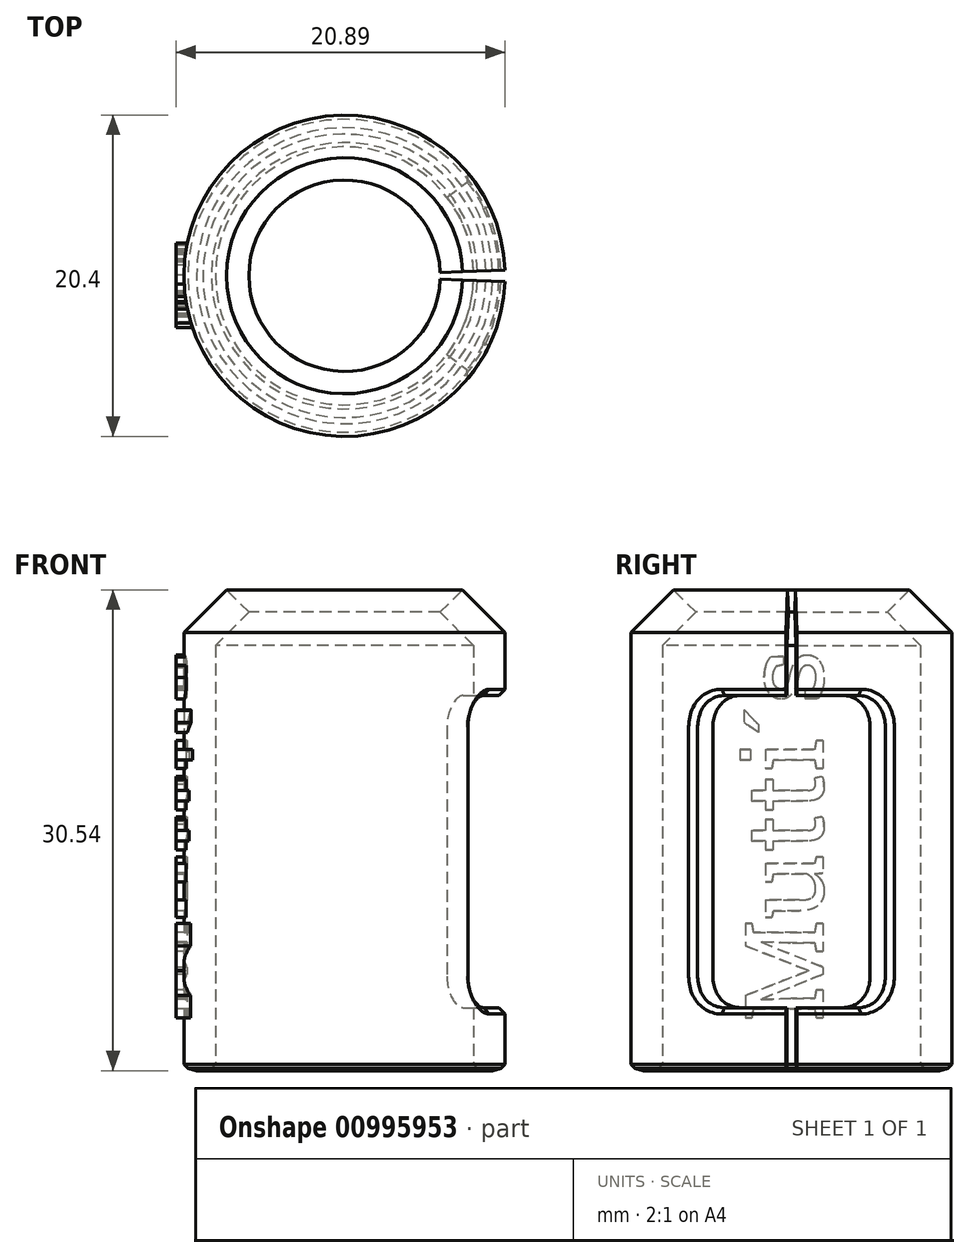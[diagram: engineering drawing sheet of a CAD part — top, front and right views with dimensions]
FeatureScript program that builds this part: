
annotation { "Feature Type Name" : "Feature", "Feature Type Description" : "" }
export const myFeature = defineFeature(function(context is Context, id is Id, definition is map)
    precondition{}
    {
        {
            var Q0;
            Q0=qCreatedBy(makeId("Front.planeOp"),FACE);
            var sketch = newSketch(context, id + "F0", { "sketchPlane" : qUnion([Q0])});
            skLineSegment(sketch, "E0", {"start": v(0, 0) * mm, "end": v(25.05, 0) * mm, "construction": true});
            skLineSegment(sketch, "E1", {"start": v(8.2, 0) * mm, "end": v(10.2, 0) * mm});
            skLineSegment(sketch, "E2", {"start": v(10.2, 0) * mm, "end": v(10.2, 27.83) * mm});
            skLineSegment(sketch, "E3", {"start": v(10.2, 27.83) * mm, "end": v(7.5, 30.54) * mm});
            skLineSegment(sketch, "E4", {"start": v(7.5, 30.54) * mm, "end": v(6.08, 29.12) * mm});
            skLineSegment(sketch, "E5", {"start": v(6.08, 29.12) * mm, "end": v(8.2, 27) * mm});
            skLineSegment(sketch, "E6", {"start": v(8.2, 27) * mm, "end": v(8.2, 0) * mm});
            skLineSegment(sketch, "E7", {"start": v(0, 0) * mm, "end": v(0, 50.76) * mm, "construction": true});
            skLineSegment(sketch, "E8", {"start": v(0, 11.1) * mm, "end": v(10.2, 11.1) * mm, "construction": true});
            skLineSegment(sketch, "E9", {"start": v(0, 11.1) * mm, "end": v(-10.2, 11.1) * mm, "construction": true});
            skLineSegment(sketch, "E10", {"start": v(-10.2, 11.1) * mm, "end": v(-20.4, 11.1) * mm, "construction": true});
            skSolve(sketch);
        }
        {
            var Q0;
            Q0 = qSketchRegion(id + "F0", true);
            var Q1;
            Q1=sQuery(id+"F0.wireOp",EDGE,"E7");
            revolve(context, id + "F1", {"surfaceOperationType" : NewSurfaceOperationType.NEW, "entities" : qUnion([Q0]), "axis" : qUnion([Q1]), "revolveType" : RevolveType.FULL});
        }
        {
            var Q0;
            Q0=qCreatedBy(makeId("Front.planeOp"),FACE);
            var sketch = newSketch(context, id + "F2", { "sketchPlane" : qUnion([Q0])});
            skLineSegment(sketch, "E11.top", {"start": v(0, 23.83) * mm, "end": v(20, 23.83) * mm});
            skLineSegment(sketch, "E11.left", {"start": v(0, 4) * mm, "end": v(0, 23.83) * mm});
            skLineSegment(sketch, "E11.right", {"start": v(20, 4) * mm, "end": v(20, 23.83) * mm});
            skLineSegment(sketch, "E12", {"start": v(0, 4) * mm, "end": v(20, 4) * mm});
            skSolve(sketch);
        }
        {
            var Q0;
            Q0 = qSketchRegion(id + "F2", true);
            var Q1;
            Q1=sQuery(id+"F2.wireOp",EDGE,"E11.left");
            revolve(context, id + "F3", {"operationType" : NewBodyOperationType.REMOVE, "surfaceOperationType" : NewSurfaceOperationType.NEW, "entities" : qUnion([Q0]), "axis" : qUnion([Q1]), "revolveType" : RevolveType.SYMMETRIC, "oppositeDirection" : true, "angle" : 75 * degree});
        }
        {
            var Q0;
            Q0=makeQuery(id+"F3.boolean.opBoolean","COPY",EDGE,{"derivedFrom":makeQuery(id+"F3.opRevolve","CAP_EDGE",EDGE,{"disambiguationData":[OSD([sQuery(id+"F2.wireOp",EDGE,"E12")])],"isStart":true})});
            var Q1;
            Q1=makeQuery(id+"F3.boolean.opBoolean","COPY",EDGE,{"derivedFrom":makeQuery(id+"F3.opRevolve","CAP_EDGE",EDGE,{"disambiguationData":[OSD([sQuery(id+"F2.wireOp",EDGE,"E12")])],"isStart":false})});
            var Q2;
            Q2=makeQuery(id+"F3.boolean.opBoolean","COPY",EDGE,{"derivedFrom":makeQuery(id+"F3.opRevolve","CAP_EDGE",EDGE,{"disambiguationData":[OSD([sQuery(id+"F2.wireOp",EDGE,"E11.top")])],"isStart":true})});
            var Q3;
            Q3=makeQuery(id+"F3.boolean.opBoolean","COPY",EDGE,{"derivedFrom":makeQuery(id+"F3.opRevolve","CAP_EDGE",EDGE,{"disambiguationData":[OSD([sQuery(id+"F2.wireOp",EDGE,"E11.top")])],"isStart":false})});
            fillet(context, id + "F4", {"entities" : qUnion([Q0, Q1, Q2, Q3]), "radius" : 2 * mm, "tangentPropagation" : true, "allowEdgeOverflow" : false});
        }
        {
            var Q0;
            Q0=qCreatedBy(makeId("Front.planeOp"),FACE);
            var sketch = newSketch(context, id + "F5", { "sketchPlane" : qUnion([Q0])});
            skLineSegment(sketch, "E13.bottom", {"start": v(0, 36.41) * mm, "end": v(18, 36.41) * mm});
            skLineSegment(sketch, "E13.top", {"start": v(0, -8.25) * mm, "end": v(18, -8.25) * mm});
            skLineSegment(sketch, "E13.left", {"start": v(0, 36.41) * mm, "end": v(0, -8.25) * mm});
            skLineSegment(sketch, "E13.right", {"start": v(18, 36.41) * mm, "end": v(18, -8.25) * mm});
            skSolve(sketch);
        }
        {
            var Q0;
            Q0 = qSketchRegion(id + "F5", true);
            var Q1;
            Q1=sQuery(id+"F0.wireOp",EDGE,"E7");
            revolve(context, id + "F6", {"operationType" : NewBodyOperationType.REMOVE, "surfaceOperationType" : NewSurfaceOperationType.NEW, "entities" : qUnion([Q0]), "axis" : qUnion([Q1]), "revolveType" : RevolveType.SYMMETRIC, "angle" : 4 * degree});
        }
        {
            var Q0;
            Q0=sQuery(id+"F0.wireOp",VERTEX,"E10.end");
            var Q1;
            Q1=sQuery(id+"F0.wireOp",VERTEX,"E8.start");
            cPlane(context, id + "F7", {"entities" : qUnion([Q0, Q1]), "cplaneType" : CPlaneType.MID_PLANE, "offset" : 25 * mm, "oppositeDirection" : true, "width" : 150 * mm, "height" : 150 * mm});
        }
        {
            var Q0;
            Q0=qCreatedBy(id+"F7.planeOp",FACE);
            var sketch = newSketch(context, id + "F8", { "sketchPlane" : qUnion([Q0])});
            skText(sketch, "E14", { "text": "Mutti´s", "fontName": "RobotoSlab-Regular.ttf"});
            skLineSegment(sketch, "E15", {"start": v(2.18, 22.14) * mm, "end": v(-9.22, 22.14) * mm, "construction": true});
            const initialGuessF8  = {"E14": [0.002, 0.00312, 0, 1, 0.005]};
            skSetInitialGuess(sketch, initialGuessF8);
            skSolve(sketch);
        }
        {
            var Q0;
            Q0 = qSketchRegion(id + "F8", true);
            extrude(context, id + "F9", {"entities" : qUnion([Q0]), "operationType" : NewBodyOperationType.ADD, "depth" : 2 * mm, "offsetDistance" : 25 * mm, "hasSecondDirection" : true, "secondDirectionOppositeDirection" : true, "secondDirectionDepth" : 0.5 * mm});
        }
        {
            var Q0;
            Q0=makeQuery(id+"F1.opRevolve","SWEPT_EDGE",EDGE,{"disambiguationData":[OSD([sQuery(id+"F0.wireOp",EDGE,"E1"),sQuery(id+"F0.wireOp",EDGE,"E2")])]});
            var Q1;
            Q1=makeQuery(id+"F1.opRevolve","SWEPT_EDGE",EDGE,{"disambiguationData":[OSD([sQuery(id+"F0.wireOp",EDGE,"E1"),sQuery(id+"F0.wireOp",EDGE,"E6")])]});
            chamfer(context, id + "F10", {"entities" : qUnion([Q0, Q1]), "width" : 0.4 * mm, "tangentPropagation" : true});
        }
        {
            var Q0;
            Q0=makeQuery(id+"F3.boolean.opBoolean","INTERSECT",EDGE,{"derivedFrom":[makeQuery(id+"F1.opRevolve","SWEPT_FACE",FACE,{"disambiguationData":[OSD([sQuery(id+"F0.wireOp",EDGE,"E2")])]}),makeQuery(id+"F3.opRevolve","CAP_FACE",FACE,{"disambiguationData":[OSD([sQuery(id+"F2.wireOp",EDGE,"E11.top"),sQuery(id+"F2.wireOp",EDGE,"E11.left"),sQuery(id+"F2.wireOp",EDGE,"E11.right"),sQuery(id+"F2.wireOp",EDGE,"E12")])],"isStart":false})]});
            var Q1;
            {var subQ0=makeQuery(id+"F1.opRevolve","SWEPT_FACE",FACE,{"disambiguationData":[OSD([sQuery(id+"F0.wireOp",EDGE,"E2")])]});var subQ1=sQuery(id+"F2.wireOp",EDGE,"E11.top");var subQ2=makeQuery(id+"F3.opRevolve","SWEPT_FACE",FACE,{"disambiguationData":[OSD([subQ1])]});Q1=makeQuery(id+"F6.boolean.opBoolean","SPLIT",EDGE,{"disambiguationData":[TD([makeQuery(id+"F4.opFillet","BLEND_FACE",FACE,{"disambiguationData":[OSD([subQ1]),TDD([makeQuery(id+"F3.boolean.opBoolean","COPY",EDGE,{"derivedFrom":makeQuery(id+"F3.opRevolve","CAP_EDGE",EDGE,{"disambiguationData":[OSD([subQ1])],"isStart":true})})])]})])],"derivedFrom":makeQuery(id+"F3.boolean.opBoolean","INTERSECT",EDGE,{"derivedFrom":[subQ0,subQ2]})});}
            chamfer(context, id + "F11", {"entities" : qUnion([Q0, Q1]), "width" : 0.4 * mm, "tangentPropagation" : true});
        }
        {
            var Q0;
            {var subQ0=sQuery(id+"F0.wireOp",EDGE,"E1");Q0=makeQuery(id+"F10.opChamfer","BLEND_EDGE",EDGE,{"blendedFrom":[makeQuery(id+"F1.opRevolve","SWEPT_EDGE",EDGE,{"disambiguationData":[OSD([subQ0,sQuery(id+"F0.wireOp",EDGE,"E2")])]}),makeQuery(id+"F1.opRevolve","SWEPT_FACE",FACE,{"disambiguationData":[OSD([subQ0])]})],"blendedInto":[makeQuery(id+"F1.opRevolve","SWEPT_FACE",FACE,{"disambiguationData":[OSD([subQ0])]})]});}
            var Q1;
            {var subQ0=sQuery(id+"F0.wireOp",EDGE,"E1");Q1=makeQuery(id+"F10.opChamfer","BLEND_EDGE",EDGE,{"blendedFrom":[makeQuery(id+"F1.opRevolve","SWEPT_EDGE",EDGE,{"disambiguationData":[OSD([subQ0,sQuery(id+"F0.wireOp",EDGE,"E6")])]}),makeQuery(id+"F1.opRevolve","SWEPT_FACE",FACE,{"disambiguationData":[OSD([subQ0])]})],"blendedInto":[makeQuery(id+"F1.opRevolve","SWEPT_FACE",FACE,{"disambiguationData":[OSD([subQ0])]})]});}
            chamfer(context, id + "F12", {"entities" : qUnion([Q0, Q1]), "chamferType" : ChamferType.TWO_OFFSETS, "width1" : 0.4 * mm, "oppositeDirection" : false, "width2" : 0.2 * mm, "tangentPropagation" : true});
        }
    });
